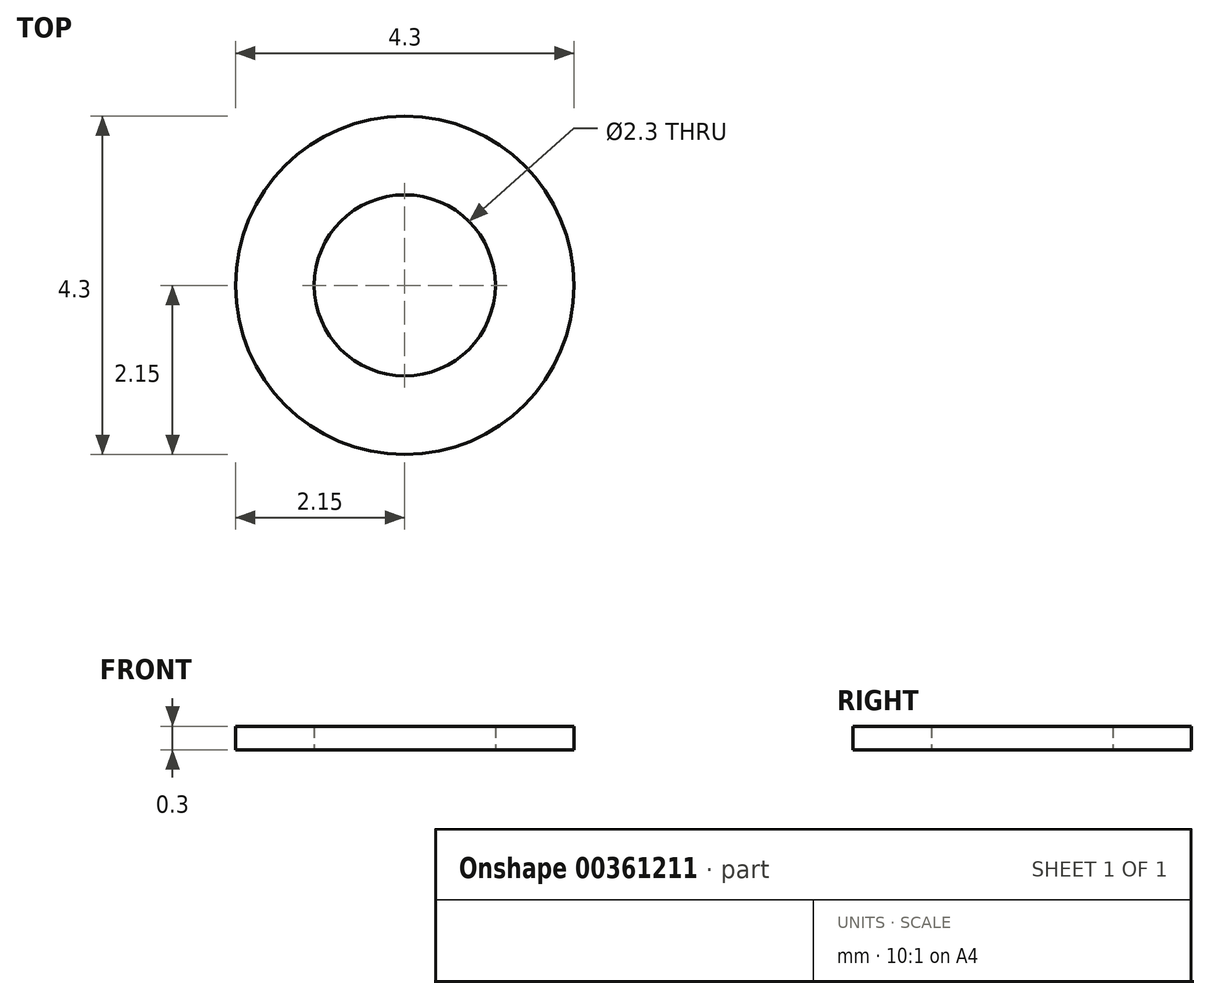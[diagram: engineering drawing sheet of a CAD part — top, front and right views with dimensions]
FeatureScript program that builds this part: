
annotation { "Feature Type Name" : "Feature", "Feature Type Description" : "" }
export const myFeature = defineFeature(function(context is Context, id is Id, definition is map)
    precondition{}
    {
        {
            var Q0;
            Q0=qCreatedBy(makeId("Top.planeOp"),FACE);
            var sketch = newSketch(context, id + "F0", { "sketchPlane" : qUnion([Q0])});
            skCircle(sketch, "E0", {"center": v(0, 0) * mm, "radius": 2.15 * mm});
            skCircle(sketch, "E1", {"center": v(0, 0) * mm, "radius": 1.15 * mm});
            skSolve(sketch);
        }
        {
            var Q0;
            Q0 = qSketchRegion(id + "F0", true);
            extrude(context, id + "F1", {"entities" : qUnion([Q0]), "depth" : 0.3 * mm, "offsetDistance" : 25 * mm});
        }
    });
